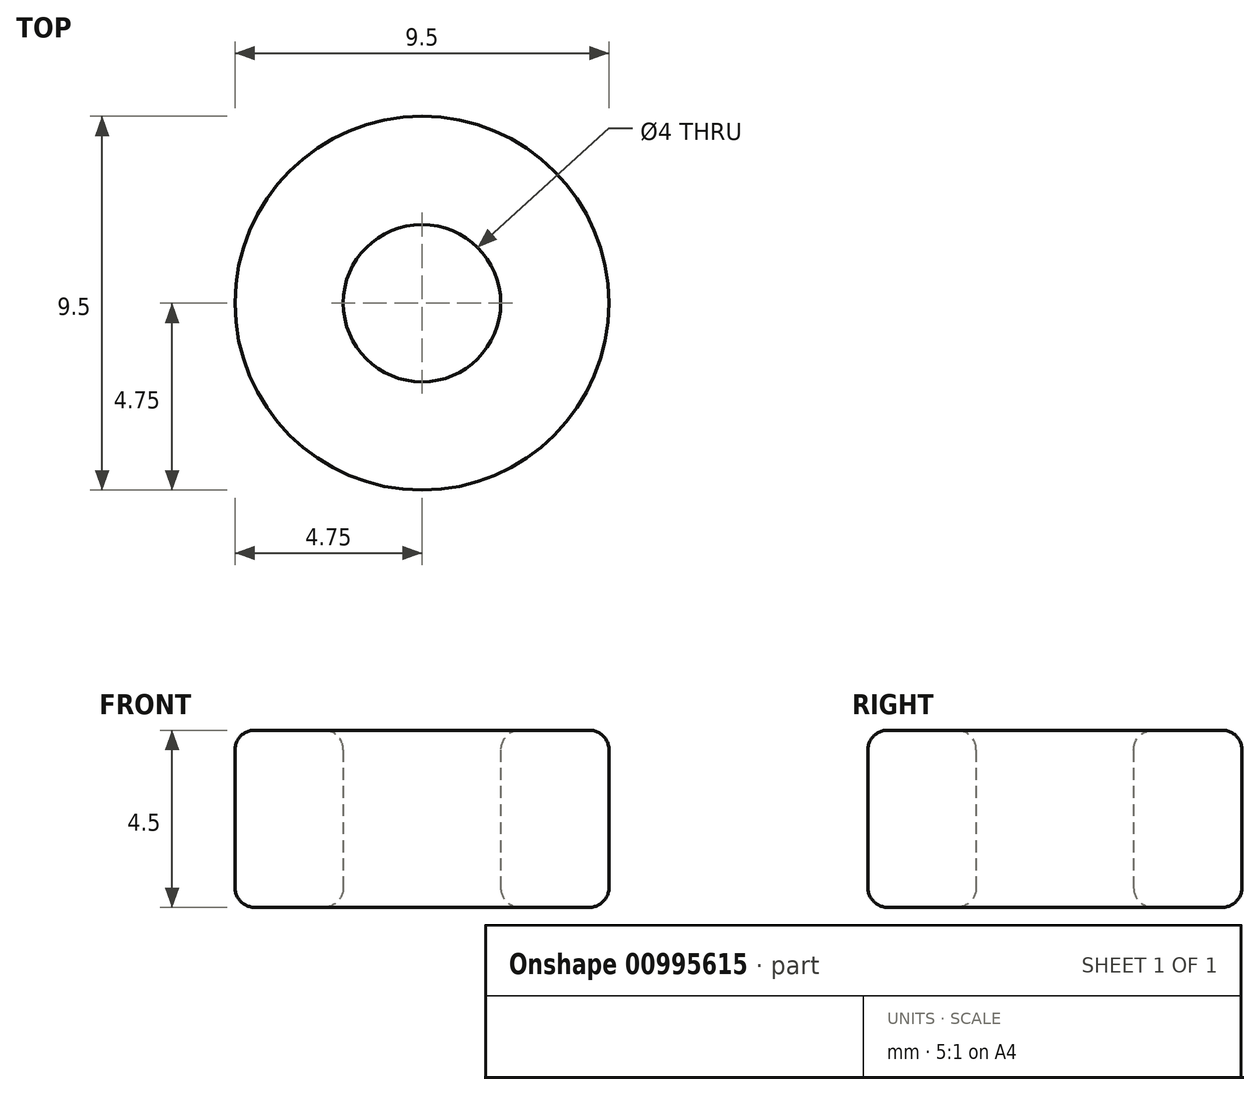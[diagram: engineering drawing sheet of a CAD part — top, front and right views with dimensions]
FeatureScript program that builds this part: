
annotation { "Feature Type Name" : "Feature", "Feature Type Description" : "" }
export const myFeature = defineFeature(function(context is Context, id is Id, definition is map)
    precondition{}
    {
        {
            var Q0;
            Q0=qCreatedBy(makeId("Top.planeOp"),FACE);
            var sketch = newSketch(context, id + "F0", { "sketchPlane" : qUnion([Q0])});
            skCircle(sketch, "E0", {"center": v(0, 0) * mm, "radius": 4.75 * mm});
            skCircle(sketch, "E1", {"center": v(0, 0) * mm, "radius": 2 * mm});
            skSolve(sketch);
        }
        {
            var Q0;
            Q0=makeQuery(id+"F0.imprint","IMPRINT",FACE,{"disambiguationData":[TD([[makeQuery(id+"F0.imprint","IMPRINT",EDGE,{"derivedFrom":sQuery(id+"F0.wireOp",EDGE,"E0")}),1.0]])]});
            extrude(context, id + "F1", {"entities" : qUnion([Q0]), "flatOperationType" : FlatOperationType.REMOVE, "depth" : 4.5 * mm, "offsetDistance" : 25 * mm, "domain" : OperationDomain.MODEL});
        }
        {
            var Q0;
            Q0=makeQuery(id+"F1.opExtrude","CAP_EDGE",EDGE,{"disambiguationData":[OSD([sQuery(id+"F0.wireOp",EDGE,"E0")])],"isStart":false});
            var Q1;
            Q1=makeQuery(id+"F1.opExtrude","CAP_EDGE",EDGE,{"disambiguationData":[OSD([sQuery(id+"F0.wireOp",EDGE,"E1")])],"isStart":false});
            var Q2;
            Q2=makeQuery(id+"F1.opExtrude","CAP_EDGE",EDGE,{"disambiguationData":[OSD([sQuery(id+"F0.wireOp",EDGE,"E1")])],"isStart":true});
            var Q3;
            Q3=makeQuery(id+"F1.opExtrude","CAP_EDGE",EDGE,{"disambiguationData":[OSD([sQuery(id+"F0.wireOp",EDGE,"E0")])],"isStart":true});
            fillet(context, id + "F2", {"entities" : qUnion([Q0, Q1, Q2, Q3]), "radius" : 0.5 * mm, "tangentPropagation" : true, "defaultsChanged" : true, "vertexSettings" : [], "allowEdgeOverflow" : false});
        }
    });
